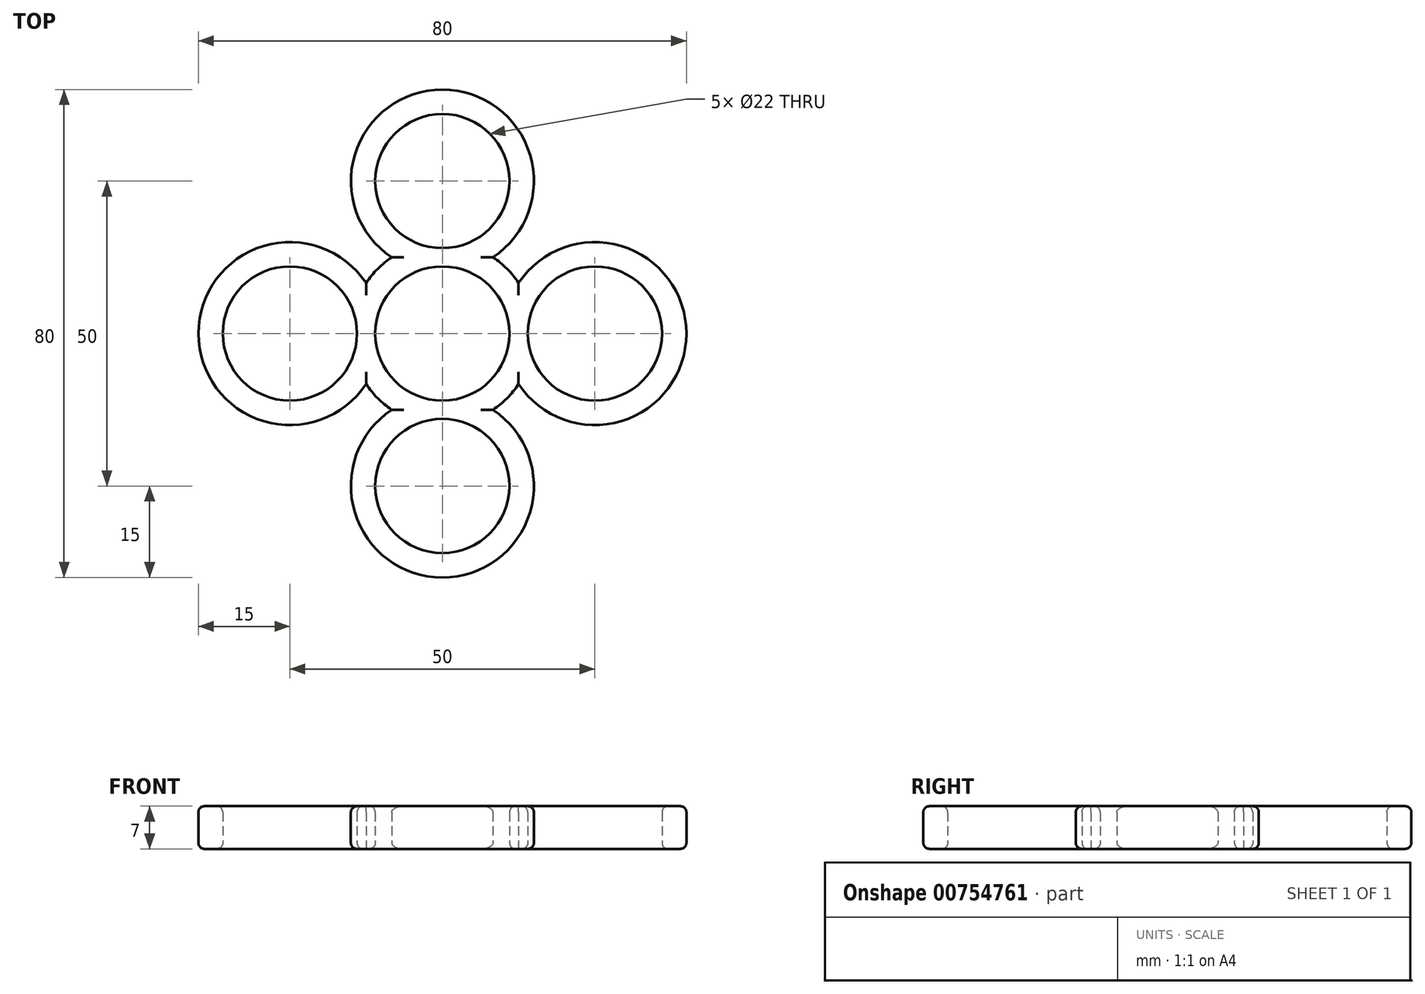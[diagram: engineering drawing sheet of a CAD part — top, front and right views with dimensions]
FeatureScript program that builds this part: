
annotation { "Feature Type Name" : "Feature", "Feature Type Description" : "" }
export const myFeature = defineFeature(function(context is Context, id is Id, definition is map)
    precondition{}
    {
        {
            var Q0;
            Q0=qCreatedBy(makeId("Top.planeOp"),FACE);
            var sketch = newSketch(context, id + "F0", { "sketchPlane" : qUnion([Q0])});
            skLineSegment(sketch, "E0", {"start": v(-11, 0) * mm, "end": v(-14, 0) * mm});
            skArc(sketch, "E1", {"start": v(-12.5, 8.3) * mm, "mid": v(-40, 0) * mm, "end": v(-12.5, -8.3) * mm});
            skCircle(sketch, "E2", {"center": v(-25, 0) * mm, "radius": 11 * mm});
            skArc(sketch, "E3.MirrorCS", {"start": v(8.3, 12.5) * mm, "mid": v(10.6, 10.6) * mm, "end": v(12.5, 8.3) * mm});
            skArc(sketch, "E4.MirrorCS", {"start": v(0, 11) * mm, "mid": v(11, 0) * mm, "end": v(0, -11) * mm});
            skCircle(sketch, "E5.MirrorC", {"center": v(25, 0) * mm, "radius": 11 * mm});
            skArc(sketch, "E6.MirrorCS", {"start": v(12.5, -8.3) * mm, "mid": v(10.6, -10.6) * mm, "end": v(8.3, -12.5) * mm});
            skArc(sketch, "E7.MirrorCS", {"start": v(12.5, 8.3) * mm, "mid": v(40, 0) * mm, "end": v(12.5, -8.3) * mm});
            skLineSegment(sketch, "E8.MirrorCS", {"start": v(0, 0) * mm, "end": v(-11, 0) * mm});
            skPoint(sketch, "E9.orphan", {"position": v(11, 0) * mm});
            skPoint(sketch, "E10.MirrorCS.end.orphan", {"position": v(-11, 0) * mm});
            skPoint(sketch, "E11.MirrorP", {"position": v(0, 11) * mm});
            skArc(sketch, "E12.MirrorCS", {"start": v(8.3, 12.5) * mm, "mid": v(0, 40) * mm, "end": v(-8.3, 12.5) * mm});
            skArc(sketch, "E13.MirrorCS", {"start": v(11, 0) * mm, "mid": v(0, 11) * mm, "end": v(-11, 0) * mm});
            skCircle(sketch, "E14.MirrorC", {"center": v(0, 25) * mm, "radius": 11 * mm});
            skArc(sketch, "E15.MirrorCS", {"start": v(-8.3, 12.5) * mm, "mid": v(-10.6, 10.6) * mm, "end": v(-12.5, 8.3) * mm});
            skPoint(sketch, "E16.MirrorP", {"position": v(0, -11) * mm});
            skArc(sketch, "E17.MirrorCS", {"start": v(0, -11) * mm, "mid": v(-11, 0) * mm, "end": v(0, 11) * mm});
            skArc(sketch, "E18.MirrorC", {"start": v(-14.58, -3.52) * mm, "mid": v(-35.85, 1.79) * mm, "end": v(-14, 0) * mm});
            skArc(sketch, "E19.MirrorCS", {"start": v(-12.5, -8.3) * mm, "mid": v(-40, 0) * mm, "end": v(-12.5, 8.3) * mm});
            skArc(sketch, "E20.MirrorCS", {"start": v(-12.5, -8.3) * mm, "mid": v(-10.6, -10.6) * mm, "end": v(-8.3, -12.5) * mm});
            skCircle(sketch, "E21.MirrorC", {"center": v(0, -25) * mm, "radius": 11 * mm});
            skArc(sketch, "E22.MirrorCS", {"start": v(-11, 0) * mm, "mid": v(0, -11) * mm, "end": v(11, 0) * mm});
            skArc(sketch, "E23.MirrorCS", {"start": v(8.3, -12.5) * mm, "mid": v(10.6, -10.6) * mm, "end": v(12.5, -8.3) * mm});
            skArc(sketch, "E24.MirrorCS", {"start": v(-8.3, -12.5) * mm, "mid": v(0, -40) * mm, "end": v(8.3, -12.5) * mm});
            skPoint(sketch, "E25.trimOffspring.end.orphan", {"position": v(-15, 0) * mm});
            skPoint(sketch, "E26.trimOffspring.end.orphan", {"position": v(0, -15) * mm});
            skArc(sketch, "E27.trimOffspring", {"start": v(-8.3, -12.5) * mm, "mid": v(-10.6, -10.6) * mm, "end": v(-12.5, -8.3) * mm});
            skPoint(sketch, "E28.trimOffspring.end.orphan", {"position": v(15, 0) * mm});
            skPoint(sketch, "E29.trimOffspring.start.orphan", {"position": v(0, 15) * mm});
            skPoint(sketch, "E30.orphan", {"position": v(-23.38, -23.38) * mm});
            skSolve(sketch);
        }
        {
            var Q0;
            Q0 = qSketchRegion(id + "F0", true);
            extrude(context, id + "F1", {"entities" : qUnion([Q0]), "depth" : 7 * mm, "offsetDistance" : 25 * mm});
        }
        {
            var Q0;
            Q0=makeQuery(id+"F1.opExtrude","CAP_EDGE",EDGE,{"disambiguationData":[OSD([sQuery(id+"F0.wireOp",EDGE,"E12.MirrorCS")])],"isStart":false});
            var Q1;
            Q1=makeQuery(id+"F1.opExtrude","CAP_EDGE",EDGE,{"disambiguationData":[OSD([sQuery(id+"F0.wireOp",EDGE,"E14.MirrorC")])],"isStart":false});
            var Q2;
            Q2=makeQuery(id+"F1.opExtrude","CAP_EDGE",EDGE,{"disambiguationData":[OSD([sQuery(id+"F0.wireOp",EDGE,"E13.MirrorCS"),sQuery(id+"F0.wireOp",EDGE,"E17.MirrorCS"),sQuery(id+"F0.wireOp",EDGE,"E22.MirrorCS")])],"isStart":false});
            var Q3;
            Q3=makeQuery(id+"F1.opExtrude","CAP_FACE",FACE,{"disambiguationData":[OSD([sQuery(id+"F0.wireOp",EDGE,"E2"),sQuery(id+"F0.wireOp",EDGE,"E3.MirrorCS"),sQuery(id+"F0.wireOp",EDGE,"E5.MirrorC"),sQuery(id+"F0.wireOp",EDGE,"E7.MirrorCS"),sQuery(id+"F0.wireOp",EDGE,"E12.MirrorCS"),sQuery(id+"F0.wireOp",EDGE,"E13.MirrorCS"),sQuery(id+"F0.wireOp",EDGE,"E14.MirrorC"),sQuery(id+"F0.wireOp",EDGE,"E15.MirrorCS"),sQuery(id+"F0.wireOp",EDGE,"E17.MirrorCS"),sQuery(id+"F0.wireOp",EDGE,"E19.MirrorCS"),sQuery(id+"F0.wireOp",EDGE,"E21.MirrorC"),sQuery(id+"F0.wireOp",EDGE,"E22.MirrorCS"),sQuery(id+"F0.wireOp",EDGE,"E23.MirrorCS"),sQuery(id+"F0.wireOp",EDGE,"E24.MirrorCS"),sQuery(id+"F0.wireOp",EDGE,"E27.trimOffspring")])],"isStart":false});
            var Q4;
            Q4=makeQuery(id+"F1.opExtrude","CAP_FACE",FACE,{"disambiguationData":[OSD([sQuery(id+"F0.wireOp",EDGE,"E2"),sQuery(id+"F0.wireOp",EDGE,"E3.MirrorCS"),sQuery(id+"F0.wireOp",EDGE,"E5.MirrorC"),sQuery(id+"F0.wireOp",EDGE,"E7.MirrorCS"),sQuery(id+"F0.wireOp",EDGE,"E12.MirrorCS"),sQuery(id+"F0.wireOp",EDGE,"E13.MirrorCS"),sQuery(id+"F0.wireOp",EDGE,"E14.MirrorC"),sQuery(id+"F0.wireOp",EDGE,"E15.MirrorCS"),sQuery(id+"F0.wireOp",EDGE,"E17.MirrorCS"),sQuery(id+"F0.wireOp",EDGE,"E19.MirrorCS"),sQuery(id+"F0.wireOp",EDGE,"E21.MirrorC"),sQuery(id+"F0.wireOp",EDGE,"E22.MirrorCS"),sQuery(id+"F0.wireOp",EDGE,"E23.MirrorCS"),sQuery(id+"F0.wireOp",EDGE,"E24.MirrorCS"),sQuery(id+"F0.wireOp",EDGE,"E27.trimOffspring")])],"isStart":true});
            fillet(context, id + "F2", {"entities" : qUnion([Q0, Q1, Q2, Q3, Q4]), "radius" : 1 * mm, "tangentPropagation" : true, "allowEdgeOverflow" : false});
        }
    });
